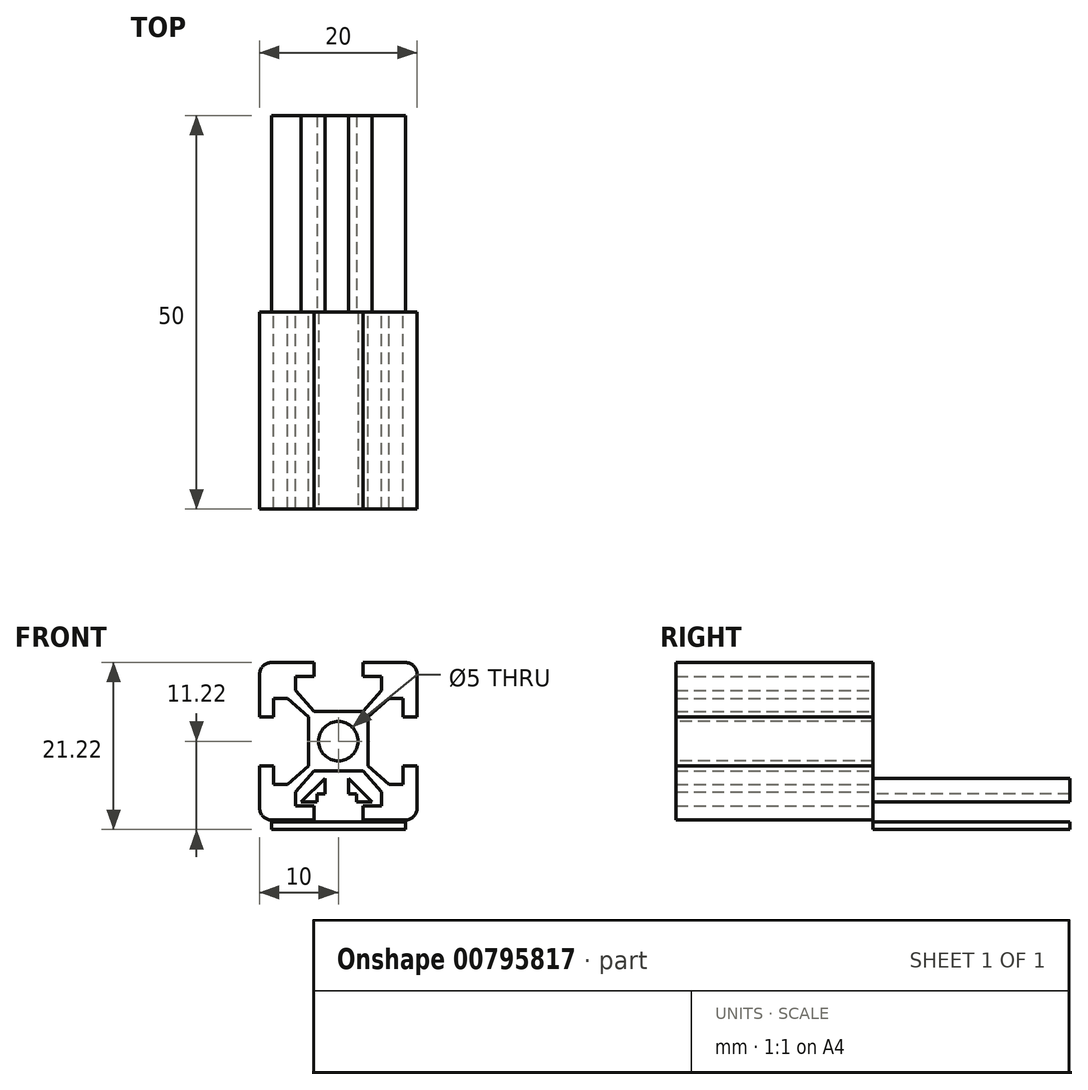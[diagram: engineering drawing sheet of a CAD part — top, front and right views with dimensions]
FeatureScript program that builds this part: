
annotation { "Feature Type Name" : "Feature", "Feature Type Description" : "" }
export const myFeature = defineFeature(function(context is Context, id is Id, definition is map)
    precondition{}
    {
        {
            var Q0;
            Q0=qCreatedBy(makeId("Front.planeOp"),FACE);
            var sketch = newSketch(context, id + "F0", { "sketchPlane" : qUnion([Q0])});
            skLineSegment(sketch, "E0.bottom", {"start": v(10, 10) * mm, "end": v(-10, 10) * mm});
            skLineSegment(sketch, "E0.top", {"start": v(10, -10) * mm, "end": v(-10, -10) * mm});
            skLineSegment(sketch, "E0.left", {"start": v(10, 10) * mm, "end": v(10, -10) * mm});
            skLineSegment(sketch, "E0.right", {"start": v(-10, 10) * mm, "end": v(-10, -10) * mm});
            skPoint(sketch, "E0.middle", {"position": v(0, 0) * mm});
            skLineSegment(sketch, "E1", {"start": v(3.11, 10) * mm, "end": v(3.11, 8.22) * mm});
            skLineSegment(sketch, "E2", {"start": v(3.11, 8.22) * mm, "end": v(5.46, 8.22) * mm});
            skLineSegment(sketch, "E3", {"start": v(5.46, 8.22) * mm, "end": v(5.46, 6.44) * mm});
            skLineSegment(sketch, "E4", {"start": v(5.46, 6.44) * mm, "end": v(3.11, 3.78) * mm});
            skLineSegment(sketch, "E5", {"start": v(3.11, 3.78) * mm, "end": v(0, 3.78) * mm});
            skLineSegment(sketch, "E6.MirrorCS", {"start": v(-3.11, 3.78) * mm, "end": v(0, 3.78) * mm});
            skLineSegment(sketch, "E7.MirrorCS", {"start": v(-5.46, 6.44) * mm, "end": v(-3.11, 3.78) * mm});
            skLineSegment(sketch, "E8.MirrorCS", {"start": v(-3.11, 10) * mm, "end": v(-3.11, 8.22) * mm});
            skLineSegment(sketch, "E9.MirrorCS", {"start": v(-5.46, 8.22) * mm, "end": v(-5.46, 6.44) * mm});
            skLineSegment(sketch, "E10.MirrorCS", {"start": v(-3.11, 8.22) * mm, "end": v(-5.46, 8.22) * mm});
            skLineSegment(sketch, "E11.1.0", {"start": v(-10, 3.11) * mm, "end": v(-8.22, 3.11) * mm});
            skLineSegment(sketch, "E11.1.1", {"start": v(-8.22, 3.11) * mm, "end": v(-8.22, 5.46) * mm});
            skLineSegment(sketch, "E11.1.2", {"start": v(-8.22, 5.46) * mm, "end": v(-6.44, 5.46) * mm});
            skLineSegment(sketch, "E11.1.3", {"start": v(-6.44, 5.46) * mm, "end": v(-3.78, 3.11) * mm});
            skLineSegment(sketch, "E11.1.4", {"start": v(-3.78, 3.11) * mm, "end": v(-3.78, 0) * mm});
            skLineSegment(sketch, "E11.1.5", {"start": v(-3.78, -3.11) * mm, "end": v(-3.78, 0) * mm});
            skLineSegment(sketch, "E11.1.6", {"start": v(-6.44, -5.46) * mm, "end": v(-3.78, -3.11) * mm});
            skLineSegment(sketch, "E11.1.7", {"start": v(-10, -3.11) * mm, "end": v(-8.22, -3.11) * mm});
            skLineSegment(sketch, "E11.1.8", {"start": v(-8.22, -5.46) * mm, "end": v(-6.44, -5.46) * mm});
            skLineSegment(sketch, "E11.1.9", {"start": v(-8.22, -3.11) * mm, "end": v(-8.22, -5.46) * mm});
            skLineSegment(sketch, "E11.2.0", {"start": v(-3.11, -10) * mm, "end": v(-3.11, -8.22) * mm});
            skLineSegment(sketch, "E11.2.1", {"start": v(-3.11, -8.22) * mm, "end": v(-5.46, -8.22) * mm});
            skLineSegment(sketch, "E11.2.2", {"start": v(-5.46, -8.22) * mm, "end": v(-5.46, -6.44) * mm});
            skLineSegment(sketch, "E11.2.3", {"start": v(-5.46, -6.44) * mm, "end": v(-3.11, -3.78) * mm});
            skLineSegment(sketch, "E11.2.4", {"start": v(-3.11, -3.78) * mm, "end": v(0, -3.78) * mm});
            skLineSegment(sketch, "E11.2.5", {"start": v(3.11, -3.78) * mm, "end": v(0, -3.78) * mm});
            skLineSegment(sketch, "E11.2.6", {"start": v(5.46, -6.44) * mm, "end": v(3.11, -3.78) * mm});
            skLineSegment(sketch, "E11.2.7", {"start": v(3.11, -10) * mm, "end": v(3.11, -8.22) * mm});
            skLineSegment(sketch, "E11.2.8", {"start": v(5.46, -8.22) * mm, "end": v(5.46, -6.44) * mm});
            skLineSegment(sketch, "E11.2.9", {"start": v(3.11, -8.22) * mm, "end": v(5.46, -8.22) * mm});
            skLineSegment(sketch, "E11.3.0", {"start": v(10, -3.11) * mm, "end": v(8.22, -3.11) * mm});
            skLineSegment(sketch, "E11.3.1", {"start": v(8.22, -3.11) * mm, "end": v(8.22, -5.46) * mm});
            skLineSegment(sketch, "E11.3.2", {"start": v(8.22, -5.46) * mm, "end": v(6.44, -5.46) * mm});
            skLineSegment(sketch, "E11.3.3", {"start": v(6.44, -5.46) * mm, "end": v(3.78, -3.11) * mm});
            skLineSegment(sketch, "E11.3.4", {"start": v(3.78, -3.11) * mm, "end": v(3.78, 0) * mm});
            skLineSegment(sketch, "E11.3.5", {"start": v(3.78, 3.11) * mm, "end": v(3.78, 0) * mm});
            skLineSegment(sketch, "E11.3.6", {"start": v(6.44, 5.46) * mm, "end": v(3.78, 3.11) * mm});
            skLineSegment(sketch, "E11.3.7", {"start": v(10, 3.11) * mm, "end": v(8.22, 3.11) * mm});
            skLineSegment(sketch, "E11.3.8", {"start": v(8.22, 5.46) * mm, "end": v(6.44, 5.46) * mm});
            skLineSegment(sketch, "E11.3.9", {"start": v(8.22, 3.11) * mm, "end": v(8.22, 5.46) * mm});
            skSolve(sketch);
        }
        {
            var Q0;
            {var subQ12=sQuery(id+"F0.wireOp",EDGE,"E1");Q0=makeQuery(id+"F0.imprint","IMPRINT",FACE,{"disambiguationData":[TD([[makeQuery(id+"F0.imprint","IMPRINT",EDGE,{"derivedFrom":subQ12}),1.0]])]});}
            extrude(context, id + "F1", {"entities" : qUnion([Q0]), "depth" : 25 * mm});
        }
        {
            var Q0;
            Q0=makeQuery(id+"F1.opExtrude","SWEPT_EDGE",EDGE,{"disambiguationData":[OSD([sQuery(id+"F0.wireOp",EDGE,"E0.bottom"),sQuery(id+"F0.wireOp",EDGE,"E0.right")])]});
            var Q1;
            Q1=makeQuery(id+"F1.opExtrude","SWEPT_EDGE",EDGE,{"disambiguationData":[OSD([sQuery(id+"F0.wireOp",EDGE,"E0.bottom"),sQuery(id+"F0.wireOp",EDGE,"E0.left")])]});
            var Q2;
            Q2=makeQuery(id+"F1.opExtrude","SWEPT_EDGE",EDGE,{"disambiguationData":[OSD([sQuery(id+"F0.wireOp",EDGE,"E0.top"),sQuery(id+"F0.wireOp",EDGE,"E0.left")])]});
            var Q3;
            Q3=makeQuery(id+"F1.opExtrude","SWEPT_EDGE",EDGE,{"disambiguationData":[OSD([sQuery(id+"F0.wireOp",EDGE,"E0.top"),sQuery(id+"F0.wireOp",EDGE,"E0.right")])]});
            fillet(context, id + "F2", {"entities" : qUnion([Q0, Q1, Q2, Q3]), "radius" : 1.5 * mm, "tangentPropagation" : true, "allowEdgeOverflow" : false});
        }
        {
            var Q0;
            Q0=makeQuery(id+"F1.opExtrude","CAP_FACE",FACE,{"disambiguationData":[OSD([sQuery(id+"F0.wireOp",EDGE,"E0.bottom"),sQuery(id+"F0.wireOp",EDGE,"E0.top"),sQuery(id+"F0.wireOp",EDGE,"E0.left"),sQuery(id+"F0.wireOp",EDGE,"E0.right"),sQuery(id+"F0.wireOp",EDGE,"E1"),sQuery(id+"F0.wireOp",EDGE,"E2"),sQuery(id+"F0.wireOp",EDGE,"E3"),sQuery(id+"F0.wireOp",EDGE,"E4"),sQuery(id+"F0.wireOp",EDGE,"E5"),sQuery(id+"F0.wireOp",EDGE,"E6.MirrorCS"),sQuery(id+"F0.wireOp",EDGE,"E7.MirrorCS"),sQuery(id+"F0.wireOp",EDGE,"E8.MirrorCS"),sQuery(id+"F0.wireOp",EDGE,"E9.MirrorCS"),sQuery(id+"F0.wireOp",EDGE,"E10.MirrorCS"),sQuery(id+"F0.wireOp",EDGE,"E11.1.0"),sQuery(id+"F0.wireOp",EDGE,"E11.1.1"),sQuery(id+"F0.wireOp",EDGE,"E11.1.2"),sQuery(id+"F0.wireOp",EDGE,"E11.1.3"),sQuery(id+"F0.wireOp",EDGE,"E11.1.4"),sQuery(id+"F0.wireOp",EDGE,"E11.1.5"),sQuery(id+"F0.wireOp",EDGE,"E11.1.6"),sQuery(id+"F0.wireOp",EDGE,"E11.1.7"),sQuery(id+"F0.wireOp",EDGE,"E11.1.8"),sQuery(id+"F0.wireOp",EDGE,"E11.1.9"),sQuery(id+"F0.wireOp",EDGE,"E11.2.0"),sQuery(id+"F0.wireOp",EDGE,"E11.2.1"),sQuery(id+"F0.wireOp",EDGE,"E11.2.2"),sQuery(id+"F0.wireOp",EDGE,"E11.2.3"),sQuery(id+"F0.wireOp",EDGE,"E11.2.4"),sQuery(id+"F0.wireOp",EDGE,"E11.2.5"),sQuery(id+"F0.wireOp",EDGE,"E11.2.6"),sQuery(id+"F0.wireOp",EDGE,"E11.2.7"),sQuery(id+"F0.wireOp",EDGE,"E11.2.8"),sQuery(id+"F0.wireOp",EDGE,"E11.2.9"),sQuery(id+"F0.wireOp",EDGE,"E11.3.0"),sQuery(id+"F0.wireOp",EDGE,"E11.3.1"),sQuery(id+"F0.wireOp",EDGE,"E11.3.2"),sQuery(id+"F0.wireOp",EDGE,"E11.3.3"),sQuery(id+"F0.wireOp",EDGE,"E11.3.4"),sQuery(id+"F0.wireOp",EDGE,"E11.3.5"),sQuery(id+"F0.wireOp",EDGE,"E11.3.6"),sQuery(id+"F0.wireOp",EDGE,"E11.3.7"),sQuery(id+"F0.wireOp",EDGE,"E11.3.8"),sQuery(id+"F0.wireOp",EDGE,"E11.3.9")])],"isStart":false});
            var sketch = newSketch(context, id + "F3", { "sketchPlane" : qUnion([Q0])});
            skCircle(sketch, "E12", {"center": v(0, 0) * mm, "radius": 2.5 * mm});
            skSolve(sketch);
        }
        {
            var Q0;
            Q0=qSketchRegion(id+"F3",true);
            var Q1;
            Q1=makeQuery(id+"F1.opExtrude","CAP_FACE",FACE,{"disambiguationData":[OSD([sQuery(id+"F0.wireOp",EDGE,"E0.bottom"),sQuery(id+"F0.wireOp",EDGE,"E0.top"),sQuery(id+"F0.wireOp",EDGE,"E0.left"),sQuery(id+"F0.wireOp",EDGE,"E0.right"),sQuery(id+"F0.wireOp",EDGE,"E1"),sQuery(id+"F0.wireOp",EDGE,"E2"),sQuery(id+"F0.wireOp",EDGE,"E3"),sQuery(id+"F0.wireOp",EDGE,"E4"),sQuery(id+"F0.wireOp",EDGE,"E5"),sQuery(id+"F0.wireOp",EDGE,"E6.MirrorCS"),sQuery(id+"F0.wireOp",EDGE,"E7.MirrorCS"),sQuery(id+"F0.wireOp",EDGE,"E8.MirrorCS"),sQuery(id+"F0.wireOp",EDGE,"E9.MirrorCS"),sQuery(id+"F0.wireOp",EDGE,"E10.MirrorCS"),sQuery(id+"F0.wireOp",EDGE,"E11.1.0"),sQuery(id+"F0.wireOp",EDGE,"E11.1.1"),sQuery(id+"F0.wireOp",EDGE,"E11.1.2"),sQuery(id+"F0.wireOp",EDGE,"E11.1.3"),sQuery(id+"F0.wireOp",EDGE,"E11.1.4"),sQuery(id+"F0.wireOp",EDGE,"E11.1.5"),sQuery(id+"F0.wireOp",EDGE,"E11.1.6"),sQuery(id+"F0.wireOp",EDGE,"E11.1.7"),sQuery(id+"F0.wireOp",EDGE,"E11.1.8"),sQuery(id+"F0.wireOp",EDGE,"E11.1.9"),sQuery(id+"F0.wireOp",EDGE,"E11.2.0"),sQuery(id+"F0.wireOp",EDGE,"E11.2.1"),sQuery(id+"F0.wireOp",EDGE,"E11.2.2"),sQuery(id+"F0.wireOp",EDGE,"E11.2.3"),sQuery(id+"F0.wireOp",EDGE,"E11.2.4"),sQuery(id+"F0.wireOp",EDGE,"E11.2.5"),sQuery(id+"F0.wireOp",EDGE,"E11.2.6"),sQuery(id+"F0.wireOp",EDGE,"E11.2.7"),sQuery(id+"F0.wireOp",EDGE,"E11.2.8"),sQuery(id+"F0.wireOp",EDGE,"E11.2.9"),sQuery(id+"F0.wireOp",EDGE,"E11.3.0"),sQuery(id+"F0.wireOp",EDGE,"E11.3.1"),sQuery(id+"F0.wireOp",EDGE,"E11.3.2"),sQuery(id+"F0.wireOp",EDGE,"E11.3.3"),sQuery(id+"F0.wireOp",EDGE,"E11.3.4"),sQuery(id+"F0.wireOp",EDGE,"E11.3.5"),sQuery(id+"F0.wireOp",EDGE,"E11.3.6"),sQuery(id+"F0.wireOp",EDGE,"E11.3.7"),sQuery(id+"F0.wireOp",EDGE,"E11.3.8"),sQuery(id+"F0.wireOp",EDGE,"E11.3.9")])],"isStart":true});
            extrude(context, id + "F4", {"entities" : qUnion([Q0]), "operationType" : NewBodyOperationType.REMOVE, "endBound" : BoundingType.UP_TO_SURFACE, "oppositeDirection" : true, "endBoundEntityFace" : qUnion([Q1]), "depth" : 25 * mm});
        }
        {
            var Q0;
            Q0=makeQuery(id+"F1.opExtrude","CAP_FACE",FACE,{"disambiguationData":[OSD([sQuery(id+"F0.wireOp",EDGE,"E0.bottom"),sQuery(id+"F0.wireOp",EDGE,"E0.top"),sQuery(id+"F0.wireOp",EDGE,"E0.left"),sQuery(id+"F0.wireOp",EDGE,"E0.right"),sQuery(id+"F0.wireOp",EDGE,"E1"),sQuery(id+"F0.wireOp",EDGE,"E2"),sQuery(id+"F0.wireOp",EDGE,"E3"),sQuery(id+"F0.wireOp",EDGE,"E4"),sQuery(id+"F0.wireOp",EDGE,"E5"),sQuery(id+"F0.wireOp",EDGE,"E6.MirrorCS"),sQuery(id+"F0.wireOp",EDGE,"E7.MirrorCS"),sQuery(id+"F0.wireOp",EDGE,"E8.MirrorCS"),sQuery(id+"F0.wireOp",EDGE,"E9.MirrorCS"),sQuery(id+"F0.wireOp",EDGE,"E10.MirrorCS"),sQuery(id+"F0.wireOp",EDGE,"E11.1.0"),sQuery(id+"F0.wireOp",EDGE,"E11.1.1"),sQuery(id+"F0.wireOp",EDGE,"E11.1.2"),sQuery(id+"F0.wireOp",EDGE,"E11.1.3"),sQuery(id+"F0.wireOp",EDGE,"E11.1.4"),sQuery(id+"F0.wireOp",EDGE,"E11.1.5"),sQuery(id+"F0.wireOp",EDGE,"E11.1.6"),sQuery(id+"F0.wireOp",EDGE,"E11.1.7"),sQuery(id+"F0.wireOp",EDGE,"E11.1.8"),sQuery(id+"F0.wireOp",EDGE,"E11.1.9"),sQuery(id+"F0.wireOp",EDGE,"E11.2.0"),sQuery(id+"F0.wireOp",EDGE,"E11.2.1"),sQuery(id+"F0.wireOp",EDGE,"E11.2.2"),sQuery(id+"F0.wireOp",EDGE,"E11.2.3"),sQuery(id+"F0.wireOp",EDGE,"E11.2.4"),sQuery(id+"F0.wireOp",EDGE,"E11.2.5"),sQuery(id+"F0.wireOp",EDGE,"E11.2.6"),sQuery(id+"F0.wireOp",EDGE,"E11.2.7"),sQuery(id+"F0.wireOp",EDGE,"E11.2.8"),sQuery(id+"F0.wireOp",EDGE,"E11.2.9"),sQuery(id+"F0.wireOp",EDGE,"E11.3.0"),sQuery(id+"F0.wireOp",EDGE,"E11.3.1"),sQuery(id+"F0.wireOp",EDGE,"E11.3.2"),sQuery(id+"F0.wireOp",EDGE,"E11.3.3"),sQuery(id+"F0.wireOp",EDGE,"E11.3.4"),sQuery(id+"F0.wireOp",EDGE,"E11.3.5"),sQuery(id+"F0.wireOp",EDGE,"E11.3.6"),sQuery(id+"F0.wireOp",EDGE,"E11.3.7"),sQuery(id+"F0.wireOp",EDGE,"E11.3.8"),sQuery(id+"F0.wireOp",EDGE,"E11.3.9")])],"isStart":true});
            var sketch = newSketch(context, id + "F5", { "sketchPlane" : qUnion([Q0])});
            skLineSegment(sketch, "E13.bottom", {"start": v(8.5, -10.22) * mm, "end": v(-8.5, -10.22) * mm});
            skLineSegment(sketch, "E13.top", {"start": v(8.5, -11.22) * mm, "end": v(-8.5, -11.22) * mm});
            skLineSegment(sketch, "E13.left", {"start": v(8.5, -10.22) * mm, "end": v(8.5, -11.22) * mm});
            skLineSegment(sketch, "E13.right", {"start": v(-8.5, -10.22) * mm, "end": v(-8.5, -11.22) * mm});
            skLineSegment(sketch, "E14.bottom", {"start": v(2.71, -10.22) * mm, "end": v(1.71, -10.22) * mm});
            skLineSegment(sketch, "E14.top", {"start": v(2.71, -6.72) * mm, "end": v(1.71, -6.72) * mm});
            skLineSegment(sketch, "E14.left", {"start": v(2.71, -10.22) * mm, "end": v(2.71, -6.72) * mm});
            skLineSegment(sketch, "E14.right", {"start": v(1.71, -10.22) * mm, "end": v(1.71, -6.72) * mm});
            skLineSegment(sketch, "E15.bottom", {"start": v(-1.29, -10.22) * mm, "end": v(-2.29, -10.22) * mm});
            skLineSegment(sketch, "E15.top", {"start": v(-1.29, -6.72) * mm, "end": v(-2.29, -6.72) * mm});
            skLineSegment(sketch, "E15.left", {"start": v(-1.29, -10.22) * mm, "end": v(-1.29, -6.72) * mm});
            skLineSegment(sketch, "E15.right", {"start": v(-2.29, -10.22) * mm, "end": v(-2.29, -6.72) * mm});
            skLineSegment(sketch, "E16", {"start": v(-2.29, -7.72) * mm, "end": v(-4.29, -7.72) * mm});
            skPoint(sketch, "E16.endSnap0", {"position": v(-4.29, -8.22) * mm});
            skLineSegment(sketch, "E17", {"start": v(-1.29, -6.72) * mm, "end": v(-1.29, -4.72) * mm});
            skLineSegment(sketch, "E18", {"start": v(-1.29, -4.72) * mm, "end": v(-4.29, -7.72) * mm});
            skLineSegment(sketch, "E19", {"start": v(2.71, -7.72) * mm, "end": v(4.71, -7.72) * mm});
            skLineSegment(sketch, "E20", {"start": v(4.71, -7.72) * mm, "end": v(1.71, -4.72) * mm});
            skLineSegment(sketch, "E21", {"start": v(1.71, -4.72) * mm, "end": v(1.71, -6.72) * mm});
            skSolve(sketch);
        }
        {
            var Q0;
            Q0=makeQuery(id+"F5.imprint","IMPRINT",FACE,{"disambiguationData":[TD([[makeQuery(id+"F5.imprint","IMPRINT",EDGE,{"derivedFrom":sQuery(id+"F5.wireOp",EDGE,"E13.top")}),-1.0]])]});
            var Q1;
            {var subQ3=sQuery(id+"F5.wireOp",EDGE,"E14.bottom");Q1=makeQuery(id+"F5.imprint","IMPRINT",FACE,{"disambiguationData":[TD([[makeQuery(id+"F5.imprint","IMPRINT",EDGE,{"derivedFrom":subQ3}),-1.0]])]});}
            var Q2;
            {var subQ1=sQuery(id+"F5.wireOp",EDGE,"E15.bottom");Q2=makeQuery(id+"F5.imprint","IMPRINT",FACE,{"disambiguationData":[TD([[makeQuery(id+"F5.imprint","IMPRINT",EDGE,{"derivedFrom":subQ1}),-1.0]])]});}
            var Q3;
            {var subQ2=sQuery(id+"F5.wireOp",EDGE,"E15.top");Q3=makeQuery(id+"F5.imprint","IMPRINT",FACE,{"disambiguationData":[TD([[makeQuery(id+"F5.imprint","IMPRINT",EDGE,{"derivedFrom":subQ2}),-1.0]])]});}
            var Q4;
            {var subQ1=sQuery(id+"F5.wireOp",EDGE,"E14.top");Q4=makeQuery(id+"F5.imprint","IMPRINT",FACE,{"disambiguationData":[TD([[makeQuery(id+"F5.imprint","IMPRINT",EDGE,{"derivedFrom":subQ1}),-1.0]])]});}
            extrude(context, id + "F6", {"entities" : qUnion([Q0, Q1, Q2, Q3, Q4]), "depth" : 25 * mm, "offsetDistance" : 25 * mm});
        }
    });
